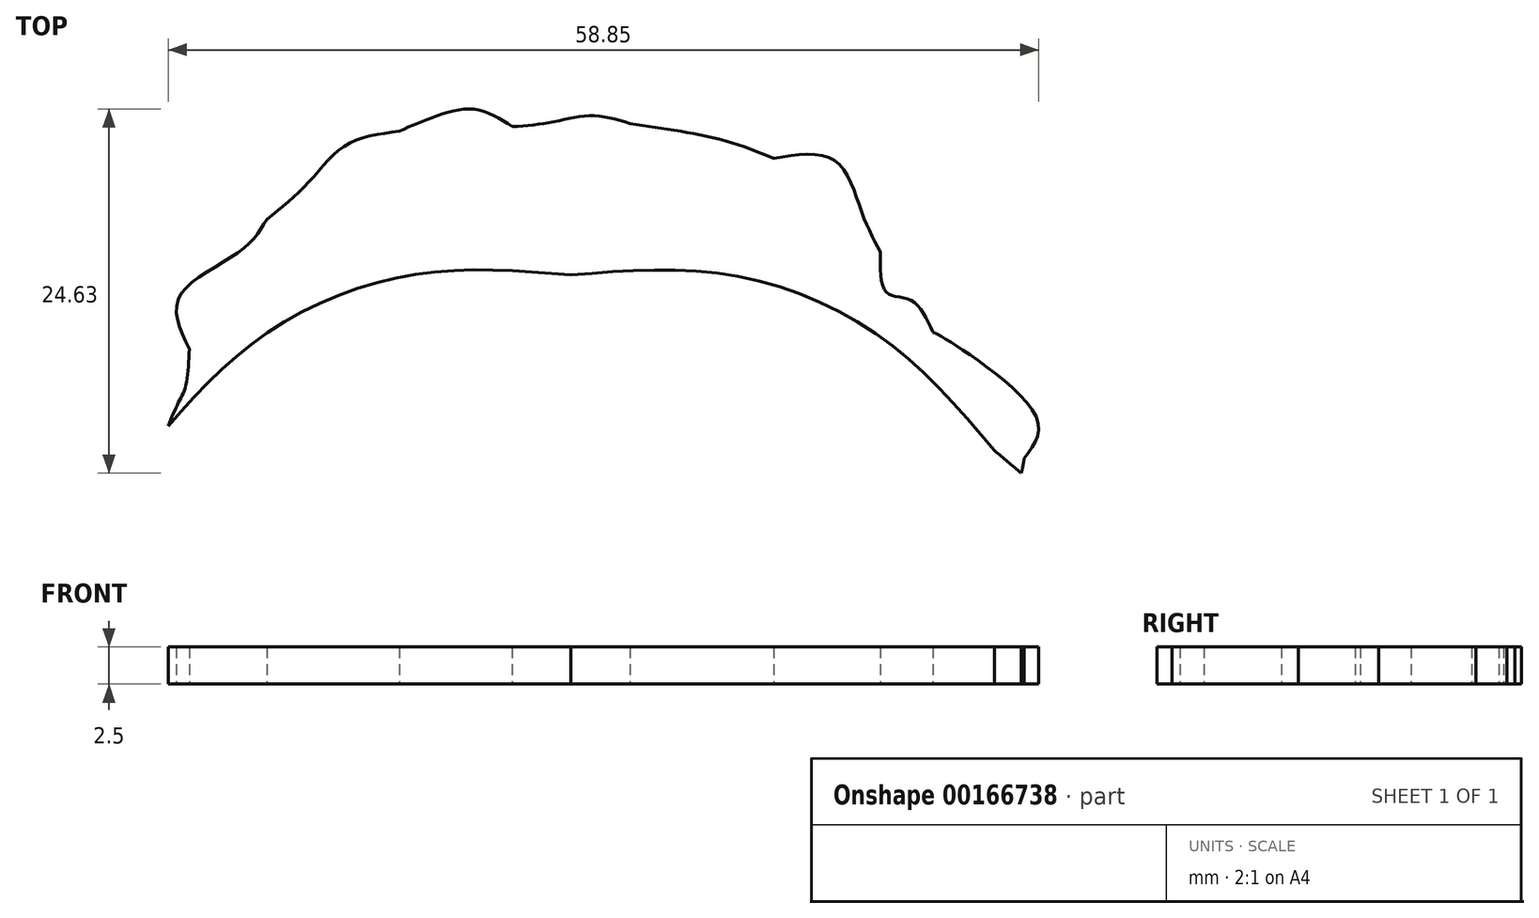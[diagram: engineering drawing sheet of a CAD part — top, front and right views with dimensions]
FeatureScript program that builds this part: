
annotation { "Feature Type Name" : "Feature", "Feature Type Description" : "" }
export const myFeature = defineFeature(function(context is Context, id is Id, definition is map)
    precondition{}
    {
        {
            var Q0;
            Q0=qCreatedBy(makeId("Top.planeOp"),FACE);
            var sketch = newSketch(context, id + "F0", { "sketchPlane" : qUnion([Q0])});
            skFitSpline(sketch, "E0", {"points": [v(-22.44, 8.06) * mm, v(-19.72, 10.4) * mm, v(-21.9, 12.2) * mm, v(-20.36, 14.03) * mm]});
            skFitSpline(sketch, "E1", {"points": [v(-20.36, 14.03) * mm, v(-19.4, 14.1) * mm, v(-19.23, 14.34) * mm, v(-18.28, 15.88) * mm]});
            skFitSpline(sketch, "E2", {"points": [v(-18.28, 15.88) * mm, v(-15.76, 17.25) * mm, v(-15.47, 19.97) * mm, v(-15.48, 22.58) * mm]});
            skFitSpline(sketch, "E3", {"points": [v(-15.48, 22.58) * mm, v(-15.49, 25.03) * mm, v(-13.17, 21.46) * mm, v(-11.65, 21.69) * mm]});
            skFitSpline(sketch, "E4", {"points": [v(-11.65, 21.69) * mm, v(-8.61, 20.47) * mm, v(-5.57, 23.05) * mm, v(-2.55, 21.9) * mm]});
            skFitSpline(sketch, "E5", {"points": [v(-2.55, 21.9) * mm, v(0.3, 21.44) * mm, v(3.14, 21.8) * mm, v(5.84, 22.71) * mm]});
            skFitSpline(sketch, "E6", {"points": [v(5.84, 22.71) * mm, v(10.2, 23.31) * mm, v(14.47, 21.95) * mm, v(18.64, 20.89) * mm]});
            skFitSpline(sketch, "E7", {"points": [v(18.64, 20.89) * mm, v(20.9, 19.25) * mm, v(18.97, 15.9) * mm, v(19.25, 13.55) * mm]});
            skFitSpline(sketch, "E8", {"points": [v(19.25, 13.55) * mm, v(18.86, 11.2) * mm, v(19.87, 5.08) * mm, v(20.68, 4.42) * mm]});
            skFitSpline(sketch, "E9", {"points": [v(20.68, 4.42) * mm, v(21, 3.48) * mm, v(23.81, 11.82) * mm, v(24.72, 11.57) * mm]});
            skFitSpline(sketch, "E10", {"points": [v(24.72, 11.57) * mm, v(28.58, 15.03) * mm, v(26.7, 16.9) * mm, v(26.25, 19.4) * mm]});
            skFitSpline(sketch, "E11", {"points": [v(26.25, 19.4) * mm, v(24.87, 21.93) * mm, v(29.68, 20.6) * mm, v(30.8, 22.5) * mm]});
            skFitSpline(sketch, "E12", {"points": [v(30.8, 22.5) * mm, v(31.7, 25.08) * mm, v(26.71, 29.78) * mm, v(24.65, 31.04) * mm]});
            skFitSpline(sketch, "E13", {"points": [v(24.65, 31.04) * mm, v(23.12, 33.2) * mm, v(21.54, 33.67) * mm, v(21.1, 36.47) * mm]});
            skFitSpline(sketch, "E14", {"points": [v(21.1, 36.47) * mm, v(19.83, 39.11) * mm, v(18.05, 42.6) * mm, v(13.89, 42.77) * mm]});
            skFitSpline(sketch, "E15", {"points": [v(13.89, 42.77) * mm, v(10.79, 43.92) * mm, v(7.39, 44.64) * mm, v(4.16, 45.13) * mm]});
            skFitSpline(sketch, "E16", {"points": [v(4.16, 45.13) * mm, v(1.53, 45.67) * mm, v(-1.08, 45.23) * mm, v(-3.8, 44.92) * mm]});
            skFitSpline(sketch, "E17", {"points": [v(-3.8, 44.92) * mm, v(-6.3, 46.09) * mm, v(-8.99, 45.62) * mm, v(-11.44, 44.6) * mm]});
            skFitSpline(sketch, "E18", {"points": [v(-11.44, 44.6) * mm, v(-15.06, 43.65) * mm, v(-17.68, 41.03) * mm, v(-20.4, 38.65) * mm]});
            skFitSpline(sketch, "E19", {"points": [v(-20.4, 38.65) * mm, v(-22.16, 36.53) * mm, v(-26.3, 33.4) * mm, v(-25.63, 29.9) * mm]});
            skFitSpline(sketch, "E20", {"points": [v(-25.63, 29.9) * mm, v(-25.91, 27.26) * mm, v(-26.45, 26.1) * mm, v(-27.5, 23.55) * mm]});
            skFitSpline(sketch, "E21", {"points": [v(-27.5, 23.55) * mm, v(-29.2, 21.64) * mm, v(-28.7, 18.17) * mm, v(-28.8, 15.86) * mm]});
            skFitSpline(sketch, "E22", {"points": [v(-28.8, 15.86) * mm, v(-29.01, 13.73) * mm, v(-29.11, 11.62) * mm, v(-28.96, 9.48) * mm]});
            skFitSpline(sketch, "E23", {"points": [v(-28.96, 9.48) * mm, v(-28.25, 8.47) * mm, v(-28.77, 9.23) * mm, v(-28.11, 7.29) * mm]});
            skFitSpline(sketch, "E24", {"points": [v(-28.11, 7.29) * mm, v(-25.53, 5.57) * mm, v(-23.38, 1.54) * mm, v(-22.44, 8.06) * mm]});
            skFitSpline(sketch, "E25", {"points": [v(18.75, 50) * mm, v(32.47, 50) * mm, v(43.5, 38.96) * mm, v(43.5, 25.25) * mm]});
            skLineSegment(sketch, "E26", {"start": v(-18.75, 50) * mm, "end": v(18.75, 50) * mm});
            skLineSegment(sketch, "E27", {"start": v(18.75, 50) * mm, "end": v(-18.75, 50) * mm});
            skFitSpline(sketch, "E28", {"points": [v(43.5, -25.25) * mm, v(43.5, -38.96) * mm, v(32.47, -50) * mm, v(18.75, -50) * mm]});
            skLineSegment(sketch, "E29", {"start": v(43.5, 25.25) * mm, "end": v(43.5, -25.25) * mm});
            skLineSegment(sketch, "E30", {"start": v(43.5, -25.25) * mm, "end": v(43.5, 25.25) * mm});
            skFitSpline(sketch, "E31", {"points": [v(-18.75, -50) * mm, v(-32.47, -50) * mm, v(-43.5, -38.96) * mm, v(-43.5, -25.25) * mm]});
            skLineSegment(sketch, "E32", {"start": v(18.75, -50) * mm, "end": v(-18.75, -50) * mm});
            skLineSegment(sketch, "E33", {"start": v(-18.75, -50) * mm, "end": v(18.75, -50) * mm});
            skFitSpline(sketch, "E34", {"points": [v(-43.5, 25.25) * mm, v(-43.5, 38.96) * mm, v(-32.47, 50) * mm, v(-18.75, 50) * mm]});
            skLineSegment(sketch, "E35", {"start": v(-43.5, -25.25) * mm, "end": v(-43.5, 25.25) * mm});
            skLineSegment(sketch, "E36", {"start": v(-43.5, 25.25) * mm, "end": v(-43.5, -25.25) * mm});
            skFitSpline(sketch, "E37", {"points": [v(40.65, -5.59) * mm, v(40.65, -27.94) * mm, v(22.53, -46.07) * mm, v(0.17, -46.07) * mm]});
            skFitSpline(sketch, "E38", {"points": [v(0.17, -46.07) * mm, v(-22.19, -46.07) * mm, v(-40.31, -27.94) * mm, v(-40.31, -5.59) * mm]});
            skFitSpline(sketch, "E39", {"points": [v(-40.31, -5.59) * mm, v(-40.31, 5.15) * mm, v(-36.05, 15.45) * mm, v(-28.46, 23.04) * mm]});
            skFitSpline(sketch, "E40", {"points": [v(-28.46, 23.04) * mm, v(-20.86, 30.63) * mm, v(-10.57, 34.9) * mm, v(0.17, 34.9) * mm]});
            skFitSpline(sketch, "E41", {"points": [v(0.17, 34.9) * mm, v(10.9, 34.9) * mm, v(21.2, 30.63) * mm, v(28.8, 23.04) * mm]});
            skFitSpline(sketch, "E42", {"points": [v(28.8, 23.04) * mm, v(36.39, 15.45) * mm, v(40.65, 5.15) * mm, v(40.65, -5.59) * mm]});
            skSolve(sketch);
        }
        {
            var Q0;
            {var subQ4=sQuery(id+"F0.wireOp",EDGE,"E12");Q0=makeQuery(id+"F0.imprint","IMPRINT",FACE,{"disambiguationData":[TD([[makeQuery(id+"F0.imprint","IMPRINT",EDGE,{"derivedFrom":subQ4}),1.0]])]});}
            var Q1;
            Q1=makeQuery(id+"F0.imprint","IMPRINT",FACE,{"disambiguationData":[TD([[makeQuery(id+"F0.imprint","IMPRINT",EDGE,{"derivedFrom":sQuery(id+"F0.wireOp",EDGE,"E0")}),1.0]])]});
            extrude(context, id + "F1", {"entities" : qUnion([Q0, Q1]), "depth" : 2.5 * mm});
        }
    });
